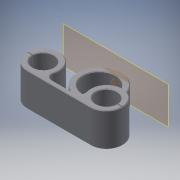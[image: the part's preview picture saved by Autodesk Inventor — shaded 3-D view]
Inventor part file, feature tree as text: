
AUTODESK INVENTOR PART (.ipt)
format: ipt  version: 2018 (Build 220112000, 112)  size: 342,528 bytes
history: native  units: mm
features: extrude x7, sketch x7, fillet x5, plane x1, chamfer x1
ambient origin geometry x8: Origin, YZ Plane, XZ Plane, XY Plane, X Axis, Y Axis, Z Axis, Center Point
bodies: Solid1 (feature_tree)
feature tree (21):
  extrude  "Extrusion1"  Depth=45.153mm
  extrude  "Extrusion2"  Depth=24.0mm TaperAngle=0.0deg
  extrude  "Extrusion3"  Depth=24.0mm TaperAngle=0.0deg
  plane  "Work Plane2"
  extrude  "Extrusion4"  Depth=4.0mm
  extrude  "Extrusion5"  Depth=26.0mm
  fillet  "Fillet1"  Radius=12.0mm
  fillet  "Fillet2"  Radius=6.5mm
  fillet  "Fillet3"  Radius=3.5mm
  chamfer  "Chamfer1"  Distance=1.0mm
  extrude  "Extrusion6"  Depth=4.0mm
  extrude  "Extrusion7"  Depth=4.0mm
  fillet  "Fillet4"  Radius=2.0mm
  fillet  "Fillet5"  Radius=0.5mm
  sketch  "Sketch1"  dims[d0=15.053mm d1=45.153mm]
  sketch  "Sketch2"  dims[d2=23.0mm d3=24.0mm d4=0.0mm]
  sketch  "Sketch4"  dims[d5=3.0mm d6=24.0mm d7=0.0mm]
  sketch  "Sketch5"  dims[d9=23.0mm d10=4.0mm]
  sketch  "Sketch6"  dims[d11=5.0mm d13=26.0mm d14=12.0mm d15=0.0mm d16=6.5mm]
  sketch  "Sketch7"  dims[d17=1.0mm d18=3.1mm d19=0.0mm d20=0.0mm d21=3.5mm d22=1.0mm d23=0.0mm]
  sketch  "Sketch8"  dims[d24=4.0mm d25=4.0mm d26=4.0mm d27=0.5mm d28=2.0mm d29=45.0deg d30=0.5mm d31=1.0mm d32=0.0mm d33=1.0mm d34=1.0mm d35=2.0mm d36=0.0mm d37=2.0mm d38=2.0mm]
